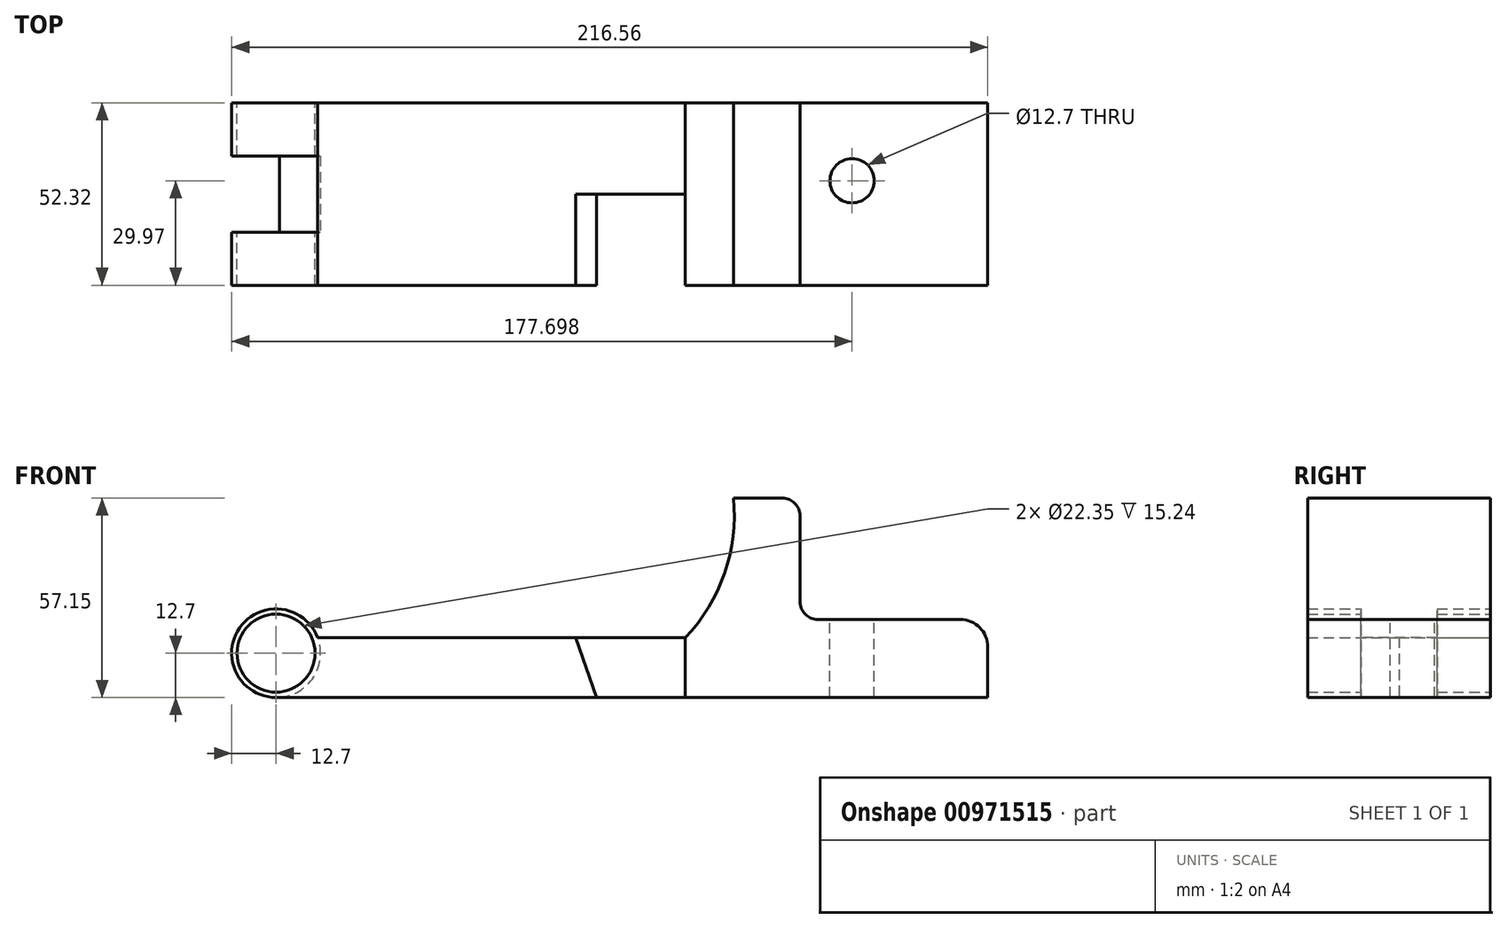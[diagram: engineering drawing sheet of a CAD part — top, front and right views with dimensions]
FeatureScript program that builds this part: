
annotation { "Feature Type Name" : "Feature", "Feature Type Description" : "" }
export const myFeature = defineFeature(function(context is Context, id is Id, definition is map)
    precondition{}
    {
        {
            var Q0;
            Q0=qCreatedBy(makeId("Front.planeOp"),FACE);
            var sketch = newSketch(context, id + "F0", { "sketchPlane" : qUnion([Q0])});
            skArc(sketch, "E0", {"start": v(11.88, 4.5) * mm, "mid": v(-10.45, 7.22) * mm, "end": v(0, -12.7) * mm});
            skCircle(sketch, "E1", {"center": v(0, 0) * mm, "radius": 11.18 * mm});
            skLineSegment(sketch, "E2.top", {"start": v(0, -12.7) * mm, "end": v(203.86, -12.7) * mm});
            skLineSegment(sketch, "E2.left", {"start": v(0, -12.7) * mm, "end": v(0, -12.7) * mm});
            skLineSegment(sketch, "E3", {"start": v(117.25, 4.5) * mm, "end": v(11.88, 4.5) * mm});
            skLineSegment(sketch, "E4", {"start": v(117.25, 4.5) * mm, "end": v(117.25, -12.7) * mm});
            skLineSegment(sketch, "E5", {"start": v(155.17, 9.65) * mm, "end": v(195.99, 9.65) * mm});
            skLineSegment(sketch, "E6", {"start": v(203.86, 1.78) * mm, "end": v(203.86, -12.7) * mm});
            skArc(sketch, "E7", {"start": v(117.25, 4.5) * mm, "mid": v(128.5, 22.97) * mm, "end": v(131.04, 44.45) * mm});
            skLineSegment(sketch, "E8", {"start": v(85.85, 4.5) * mm, "end": v(91.85, -12.7) * mm});
            skLineSegment(sketch, "E9", {"start": v(131.04, 44.45) * mm, "end": v(145, 44.45) * mm});
            skLineSegment(sketch, "E10", {"start": v(150.09, 39.37) * mm, "end": v(150.09, 14.73) * mm});
            skArc(sketch, "E11.filletArc", {"start": v(150.09, 14.73) * mm, "mid": v(151.58, 11.14) * mm, "end": v(155.17, 9.65) * mm});
            skPoint(sketch, "E12.visualSharp", {"position": v(150.09, 44.45) * mm});
            skArc(sketch, "E12.filletArc", {"start": v(150.09, 39.37) * mm, "mid": v(148.6, 42.96) * mm, "end": v(145, 44.45) * mm});
            skPoint(sketch, "E13.visualSharp", {"position": v(203.86, 9.65) * mm});
            skArc(sketch, "E13.filletArc", {"start": v(203.86, 1.78) * mm, "mid": v(201.55, 7.35) * mm, "end": v(195.99, 9.65) * mm});
            skLineSegment(sketch, "E14", {"start": v(203.86, 1.78) * mm, "end": v(117.25, 1.78) * mm});
            skSolve(sketch);
        }
        {
            var Q0;
            {var subQ1=sQuery(id+"F0.wireOp",EDGE,"E0");Q0=makeQuery(id+"F0.imprint","IMPRINT",FACE,{"disambiguationData":[TD([[makeQuery(id+"F0.imprint","IMPRINT",EDGE,{"derivedFrom":subQ1}),1.0]])]});}
            var Q1;
            {var subQ0=sQuery(id+"F0.wireOp",EDGE,"E4");Q1=makeQuery(id+"F0.imprint","IMPRINT",FACE,{"disambiguationData":[TD([[makeQuery(id+"F0.imprint","IMPRINT",EDGE,{"derivedFrom":subQ0}),-1.0]])]});}
            var Q2;
            {var subQ0=sQuery(id+"F0.wireOp",EDGE,"E4");Q2=makeQuery(id+"F0.imprint","IMPRINT",FACE,{"disambiguationData":[TD([[makeQuery(id+"F0.imprint","IMPRINT",EDGE,{"derivedFrom":subQ0}),1.0]])]});}
            var Q3;
            Q3=makeQuery(id+"F0.imprint","IMPRINT",FACE,{"disambiguationData":[TD([[makeQuery(id+"F0.imprint","IMPRINT",EDGE,{"derivedFrom":sQuery(id+"F0.wireOp",EDGE,"E5")}),-1.0]])]});
            extrude(context, id + "F1", {"entities" : qUnion([Q0, Q1, Q2, Q3]), "endBound" : BoundingType.SYMMETRIC, "depth" : 52.32 * mm, "offsetDistance" : 25.4 * mm});
        }
        {
            var Q0;
            {var subQ0=sQuery(id+"F0.wireOp",EDGE,"E4");Q0=makeQuery(id+"F0.imprint","IMPRINT",FACE,{"disambiguationData":[TD([[makeQuery(id+"F0.imprint","IMPRINT",EDGE,{"derivedFrom":subQ0}),-1.0]])]});}
            extrude(context, id + "F2", {"entities" : qUnion([Q0]), "operationType" : NewBodyOperationType.REMOVE, "endBound" : BoundingType.THROUGH_ALL, "depth" : 25.4 * mm, "offsetDistance" : 25.4 * mm});
        }
        {
            var Q0;
            Q0=qCreatedBy(makeId("Front.planeOp"),FACE);
            var sketch = newSketch(context, id + "F3", { "sketchPlane" : qUnion([Q0])});
            skCircle(sketch, "E15", {"center": v(0, 0) * mm, "radius": 12.74 * mm});
            skSolve(sketch);
        }
        {
            var Q0;
            Q0 = qSketchRegion(id + "F3", true);
            extrude(context, id + "F4", {"entities" : qUnion([Q0]), "operationType" : NewBodyOperationType.REMOVE, "endBound" : BoundingType.SYMMETRIC, "oppositeDirection" : true, "depth" : 21.84 * mm, "offsetDistance" : 25.4 * mm});
        }
        {
            var Q0;
            Q0=makeQuery(id+"F1.opExtrude","SWEPT_FACE",FACE,{"disambiguationData":[OSD([sQuery(id+"F0.wireOp",EDGE,"E5")])]});
            var sketch = newSketch(context, id + "F5", { "sketchPlane" : qUnion([Q0])});
            skCircle(sketch, "E16", {"center": v(165, 3.81) * mm, "radius": 6.35 * mm});
            skSolve(sketch);
        }
        {
            var Q0;
            Q0 = qSketchRegion(id + "F5", true);
            extrude(context, id + "F6", {"entities" : qUnion([Q0]), "operationType" : NewBodyOperationType.REMOVE, "endBound" : BoundingType.THROUGH_ALL, "oppositeDirection" : true, "depth" : 25.4 * mm, "offsetDistance" : 25.4 * mm});
        }
    });
